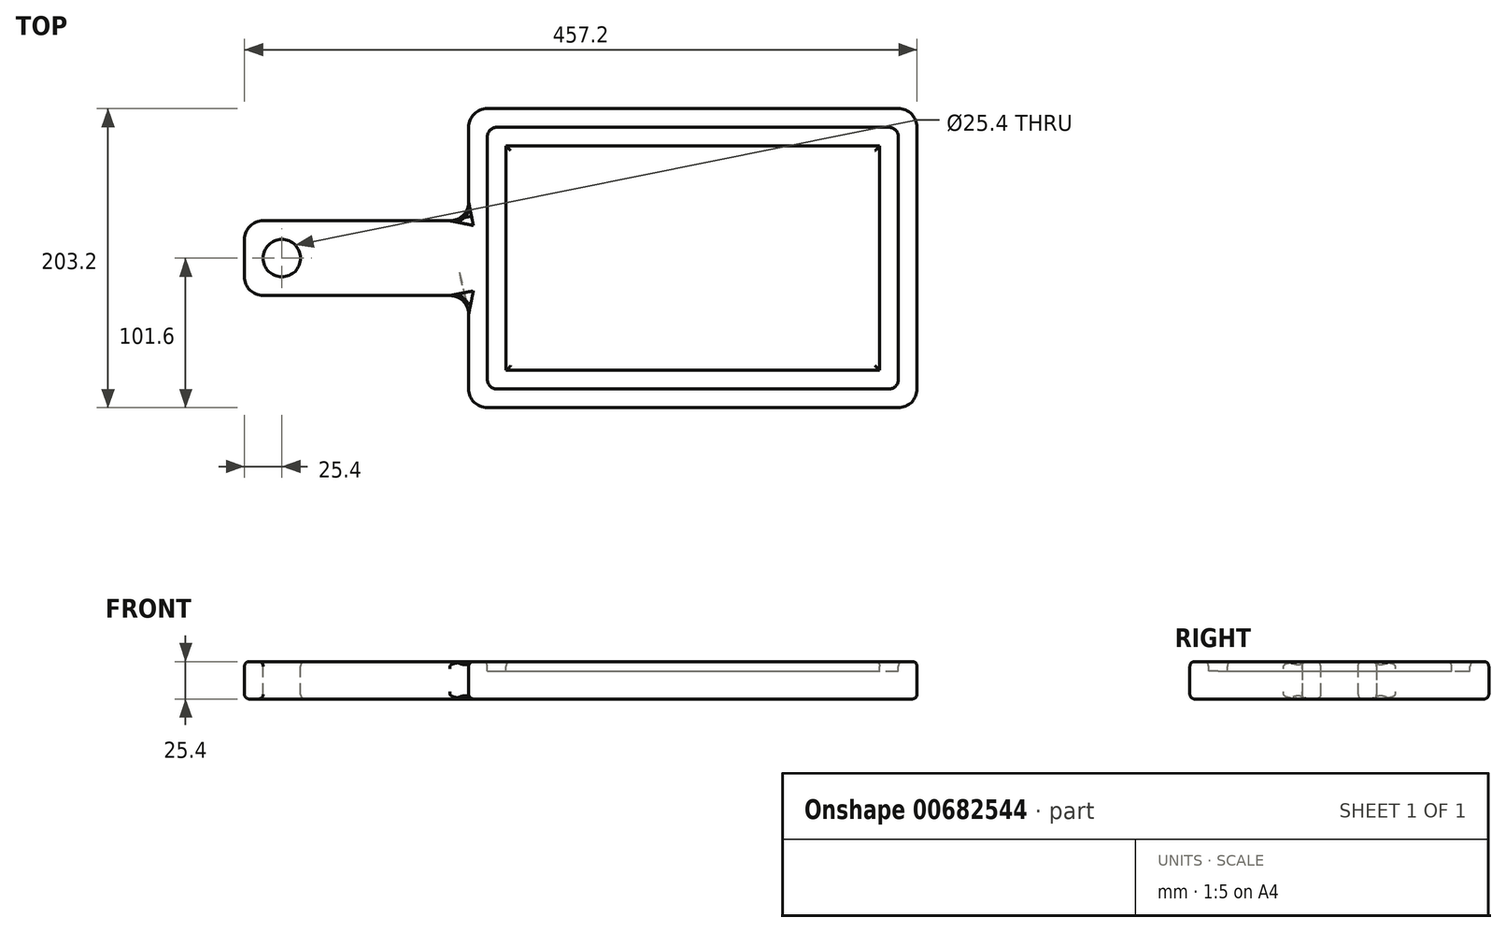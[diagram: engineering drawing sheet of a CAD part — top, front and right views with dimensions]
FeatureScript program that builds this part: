
annotation { "Feature Type Name" : "Feature", "Feature Type Description" : "" }
export const myFeature = defineFeature(function(context is Context, id is Id, definition is map)
    precondition{}
    {
        {
            var Q0;
            Q0=qCreatedBy(makeId("Top.planeOp"),FACE);
            var sketch = newSketch(context, id + "F0", { "sketchPlane" : qUnion([Q0])});
            skLineSegment(sketch, "E0.bottom", {"start": v(0, 0) * mm, "end": v(304.8, 0) * mm});
            skLineSegment(sketch, "E0.top", {"start": v(0, 203.2) * mm, "end": v(304.8, 203.2) * mm});
            skLineSegment(sketch, "E0.left", {"start": v(0, 0) * mm, "end": v(0, 203.2) * mm});
            skLineSegment(sketch, "E0.right", {"start": v(304.8, 0) * mm, "end": v(304.8, 203.2) * mm});
            skLineSegment(sketch, "E1.bottom", {"start": v(0, 127) * mm, "end": v(-152.4, 127) * mm});
            skLineSegment(sketch, "E1.top", {"start": v(0, 76.2) * mm, "end": v(-152.4, 76.2) * mm});
            skLineSegment(sketch, "E1.left", {"start": v(0, 127) * mm, "end": v(0, 76.2) * mm});
            skLineSegment(sketch, "E1.right", {"start": v(-152.4, 127) * mm, "end": v(-152.4, 76.2) * mm});
            skSolve(sketch);
        }
        {
            var Q0;
            {var subQ3=sQuery(id+"F0.wireOp",EDGE,"E0.bottom");Q0=makeQuery(id+"F0.imprint","IMPRINT",FACE,{"disambiguationData":[TD([[makeQuery(id+"F0.imprint","IMPRINT",EDGE,{"derivedFrom":subQ3}),1.0]])]});}
            var Q1;
            Q1=makeQuery(id+"F0.imprint","IMPRINT",FACE,{"disambiguationData":[TD([[makeQuery(id+"F0.imprint","IMPRINT",EDGE,{"derivedFrom":sQuery(id+"F0.wireOp",EDGE,"E1.bottom")}),1.0]])]});
            extrude(context, id + "F1", {"entities" : qUnion([Q0, Q1]), "depth" : 25.4 * mm, "offsetDistance" : 25.4 * mm});
        }
        {
            var Q0;
            Q0=makeQuery(id+"F1.opExtrude","CAP_FACE",FACE,{"disambiguationData":[OSD([sQuery(id+"F0.wireOp",EDGE,"E0.bottom"),sQuery(id+"F0.wireOp",EDGE,"E0.top"),sQuery(id+"F0.wireOp",EDGE,"E0.left"),sQuery(id+"F0.wireOp",EDGE,"E0.right"),sQuery(id+"F0.wireOp",EDGE,"E1.bottom"),sQuery(id+"F0.wireOp",EDGE,"E1.top"),sQuery(id+"F0.wireOp",EDGE,"E1.right")])],"isStart":false});
            var sketch = newSketch(context, id + "F2", { "sketchPlane" : qUnion([Q0])});
            skCircle(sketch, "E2", {"center": v(-127, 101.6) * mm, "radius": 12.7 * mm});
            skSolve(sketch);
        }
        {
            var Q0;
            Q0 = qSketchRegion(id + "F2", true);
            extrude(context, id + "F3", {"entities" : qUnion([Q0]), "operationType" : NewBodyOperationType.REMOVE, "oppositeDirection" : true, "depth" : 25.4 * mm, "offsetDistance" : 25.4 * mm});
        }
        {
            var Q0;
            Q0=makeQuery(id+"F1.opExtrude","CAP_FACE",FACE,{"disambiguationData":[OSD([sQuery(id+"F0.wireOp",EDGE,"E0.bottom"),sQuery(id+"F0.wireOp",EDGE,"E0.top"),sQuery(id+"F0.wireOp",EDGE,"E0.left"),sQuery(id+"F0.wireOp",EDGE,"E0.right"),sQuery(id+"F0.wireOp",EDGE,"E1.bottom"),sQuery(id+"F0.wireOp",EDGE,"E1.top"),sQuery(id+"F0.wireOp",EDGE,"E1.right")])],"isStart":false});
            var sketch = newSketch(context, id + "F4", { "sketchPlane" : qUnion([Q0])});
            skLineSegment(sketch, "E3.0", {"start": v(12.7, 12.7) * mm, "end": v(12.7, 76.2) * mm});
            skLineSegment(sketch, "E3.1", {"start": v(12.7, 127) * mm, "end": v(12.7, 190.5) * mm});
            skLineSegment(sketch, "E3.2", {"start": v(12.7, 190.5) * mm, "end": v(292.1, 190.5) * mm});
            skLineSegment(sketch, "E3.3", {"start": v(292.1, 12.7) * mm, "end": v(292.1, 190.5) * mm});
            skLineSegment(sketch, "E3.4", {"start": v(12.7, 12.7) * mm, "end": v(292.1, 12.7) * mm});
            skLineSegment(sketch, "E4", {"start": v(12.7, 127) * mm, "end": v(12.7, 76.2) * mm});
            skLineSegment(sketch, "E5.0", {"start": v(25.4, 127) * mm, "end": v(25.4, 177.8) * mm});
            skLineSegment(sketch, "E5.1", {"start": v(279.4, 25.4) * mm, "end": v(279.4, 177.8) * mm});
            skLineSegment(sketch, "E5.2", {"start": v(25.4, 25.4) * mm, "end": v(279.4, 25.4) * mm});
            skLineSegment(sketch, "E5.3", {"start": v(25.4, 177.8) * mm, "end": v(279.4, 177.8) * mm});
            skLineSegment(sketch, "E5.4", {"start": v(25.4, 25.4) * mm, "end": v(25.4, 76.2) * mm});
            skLineSegment(sketch, "E5.5", {"start": v(25.4, 127) * mm, "end": v(25.4, 76.2) * mm});
            skSolve(sketch);
        }
        {
            var Q0;
            Q0=makeQuery(id+"F4.imprint","IMPRINT",FACE,{"disambiguationData":[TD([[makeQuery(id+"F4.imprint","IMPRINT",EDGE,{"derivedFrom":sQuery(id+"F4.wireOp",EDGE,"E3.0")}),-1.0]])]});
            extrude(context, id + "F5", {"entities" : qUnion([Q0]), "operationType" : NewBodyOperationType.REMOVE, "oppositeDirection" : true, "depth" : 6.35 * mm, "offsetDistance" : 25.4 * mm});
        }
        {
            var Q0;
            Q0=makeQuery(id+"F5.boolean.opBoolean","COPY",EDGE,{"derivedFrom":makeQuery(id+"F5.opExtrude","SWEPT_EDGE",EDGE,{"disambiguationData":[OSD([sQuery(id+"F4.wireOp",EDGE,"E3.1"),sQuery(id+"F4.wireOp",EDGE,"E3.2")])]})});
            var Q1;
            Q1=makeQuery(id+"F5.boolean.opBoolean","COPY",EDGE,{"derivedFrom":makeQuery(id+"F5.opExtrude","SWEPT_EDGE",EDGE,{"disambiguationData":[OSD([sQuery(id+"F4.wireOp",EDGE,"E3.2"),sQuery(id+"F4.wireOp",EDGE,"E3.3")])]})});
            var Q2;
            Q2=makeQuery(id+"F5.boolean.opBoolean","COPY",EDGE,{"derivedFrom":makeQuery(id+"F5.opExtrude","SWEPT_EDGE",EDGE,{"disambiguationData":[OSD([sQuery(id+"F4.wireOp",EDGE,"E3.3"),sQuery(id+"F4.wireOp",EDGE,"E3.4")])]})});
            var Q3;
            Q3=makeQuery(id+"F5.boolean.opBoolean","COPY",EDGE,{"derivedFrom":makeQuery(id+"F5.opExtrude","SWEPT_EDGE",EDGE,{"disambiguationData":[OSD([sQuery(id+"F4.wireOp",EDGE,"E3.0"),sQuery(id+"F4.wireOp",EDGE,"E3.4")])]})});
            fillet(context, id + "F6", {"entities" : qUnion([Q0, Q1, Q2, Q3]), "radius" : 6.35 * mm, "tangentPropagation" : true, "allowEdgeOverflow" : false});
        }
        {
            var Q0;
            Q0=makeQuery(id+"F1.opExtrude","SWEPT_EDGE",EDGE,{"disambiguationData":[OSD([sQuery(id+"F0.wireOp",EDGE,"E1.top"),sQuery(id+"F0.wireOp",EDGE,"E1.right")])]});
            var Q1;
            Q1=makeQuery(id+"F1.opExtrude","SWEPT_EDGE",EDGE,{"disambiguationData":[OSD([sQuery(id+"F0.wireOp",EDGE,"E0.bottom"),sQuery(id+"F0.wireOp",EDGE,"E0.left")])]});
            var Q2;
            Q2=makeQuery(id+"F1.opExtrude","SWEPT_EDGE",EDGE,{"disambiguationData":[OSD([sQuery(id+"F0.wireOp",EDGE,"E0.bottom"),sQuery(id+"F0.wireOp",EDGE,"E0.right")])]});
            var Q3;
            Q3=makeQuery(id+"F1.opExtrude","SWEPT_EDGE",EDGE,{"disambiguationData":[OSD([sQuery(id+"F0.wireOp",EDGE,"E0.top"),sQuery(id+"F0.wireOp",EDGE,"E0.right")])]});
            var Q4;
            Q4=makeQuery(id+"F1.opExtrude","SWEPT_EDGE",EDGE,{"disambiguationData":[OSD([sQuery(id+"F0.wireOp",EDGE,"E0.top"),sQuery(id+"F0.wireOp",EDGE,"E0.left")])]});
            var Q5;
            Q5=makeQuery(id+"F1.opExtrude","SWEPT_EDGE",EDGE,{"disambiguationData":[OSD([sQuery(id+"F0.wireOp",EDGE,"E1.bottom"),sQuery(id+"F0.wireOp",EDGE,"E1.right")])]});
            fillet(context, id + "F7", {"entities" : qUnion([Q0, Q1, Q2, Q3, Q4, Q5]), "radius" : 12.7 * mm, "tangentPropagation" : true, "allowEdgeOverflow" : false});
        }
        {
            var Q0;
            Q0=makeQuery(id+"F5.boolean.opBoolean","SPLIT",FACE,{"disambiguationData":[TD([makeQuery(id+"F5.opExtrude","SWEPT_FACE",FACE,{"disambiguationData":[OSD([sQuery(id+"F4.wireOp",EDGE,"E5.1")])]})])],"derivedFrom":makeQuery(id+"F1.opExtrude","CAP_FACE",FACE,{"disambiguationData":[OSD([sQuery(id+"F0.wireOp",EDGE,"E0.bottom"),sQuery(id+"F0.wireOp",EDGE,"E0.top"),sQuery(id+"F0.wireOp",EDGE,"E0.left"),sQuery(id+"F0.wireOp",EDGE,"E0.right"),sQuery(id+"F0.wireOp",EDGE,"E1.bottom"),sQuery(id+"F0.wireOp",EDGE,"E1.top"),sQuery(id+"F0.wireOp",EDGE,"E1.right")])],"isStart":false})});
            var Q1;
            {var subQ0=sQuery(id+"F0.wireOp",EDGE,"E1.right");var subQ1=sQuery(id+"F0.wireOp",EDGE,"E1.top");var subQ2=sQuery(id+"F0.wireOp",EDGE,"E1.bottom");var subQ3=sQuery(id+"F0.wireOp",EDGE,"E0.right");var subQ4=sQuery(id+"F0.wireOp",EDGE,"E0.bottom");var subQ5=sQuery(id+"F0.wireOp",EDGE,"E0.left");var subQ6=sQuery(id+"F0.wireOp",EDGE,"E0.top");Q1=makeQuery(id+"F5.boolean.opBoolean","SPLIT",FACE,{"disambiguationData":[TD([makeQuery(id+"F1.opExtrude","SWEPT_FACE",FACE,{"disambiguationData":[OSD([subQ4])]})])],"derivedFrom":makeQuery(id+"F1.opExtrude","CAP_FACE",FACE,{"disambiguationData":[OSD([subQ4,subQ6,subQ5,subQ3,subQ2,subQ1,subQ0])],"isStart":false})});}
            var Q2;
            Q2=makeQuery(id+"F1.opExtrude","CAP_FACE",FACE,{"disambiguationData":[OSD([sQuery(id+"F0.wireOp",EDGE,"E0.bottom"),sQuery(id+"F0.wireOp",EDGE,"E0.top"),sQuery(id+"F0.wireOp",EDGE,"E0.left"),sQuery(id+"F0.wireOp",EDGE,"E0.right"),sQuery(id+"F0.wireOp",EDGE,"E1.bottom"),sQuery(id+"F0.wireOp",EDGE,"E1.top"),sQuery(id+"F0.wireOp",EDGE,"E1.right")])],"isStart":true});
            fillet(context, id + "F8", {"entities" : qUnion([Q0, Q1, Q2]), "radius" : 3.17 * mm, "tangentPropagation" : true, "allowEdgeOverflow" : false});
        }
        {
            var Q0;
            Q0=makeQuery(id+"F1.opExtrude","SWEPT_EDGE",EDGE,{"disambiguationData":[OSD([sQuery(id+"F0.wireOp",EDGE,"E0.left"),sQuery(id+"F0.wireOp",EDGE,"E1.bottom"),sQuery(id+"F0.wireOp",EDGE,"E1.left")])]});
            fillet(context, id + "F9", {"entities" : qUnion([Q0]), "radius" : 12.7 * mm, "tangentPropagation" : true, "allowEdgeOverflow" : false});
        }
        {
            var Q0;
            {var subQ0=sQuery(id+"F0.wireOp",EDGE,"E1.top");var subQ1=sQuery(id+"F0.wireOp",EDGE,"E0.left");Q0=makeQuery(id+"F8.opFillet","BLEND_EDGE",EDGE,{"blendedFrom":[makeQuery(id+"F1.opExtrude","CAP_EDGE",EDGE,{"disambiguationData":[OSD([subQ1]),TDD([makeQuery(id+"F0.imprint","IMPRINT",EDGE,{"disambiguationData":[TD([[makeQuery(id+"F0.imprint","INTERSECT",VERTEX,{"derivedFrom":[sQuery(id+"F0.wireOp",EDGE,"E0.bottom"),subQ1]}),-1.0]])],"derivedFrom":subQ1})])],"isStart":false}),makeQuery(id+"F1.opExtrude","CAP_EDGE",EDGE,{"disambiguationData":[OSD([subQ0])],"isStart":false})],"blendedInto":[]});}
            fillet(context, id + "F10", {"entities" : qUnion([Q0]), "radius" : 12.7 * mm, "tangentPropagation" : true, "allowEdgeOverflow" : false});
        }
    });
